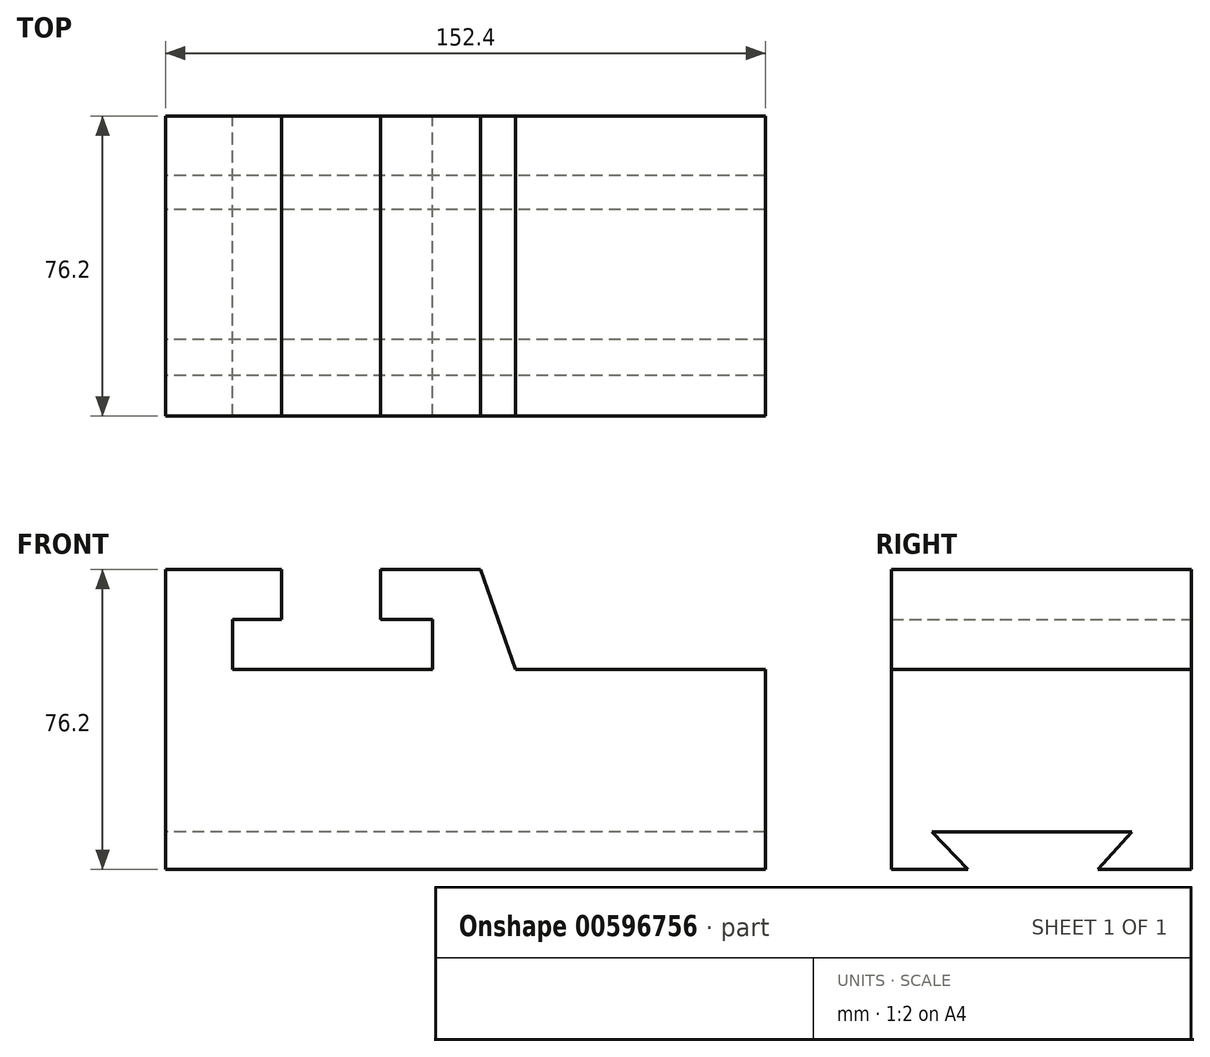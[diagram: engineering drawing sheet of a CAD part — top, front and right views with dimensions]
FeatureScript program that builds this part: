
annotation { "Feature Type Name" : "Feature", "Feature Type Description" : "" }
export const myFeature = defineFeature(function(context is Context, id is Id, definition is map)
    precondition{}
    {
        {
            var Q0;
            Q0=qCreatedBy(makeId("Front.planeOp"),FACE);
            var sketch = newSketch(context, id + "F0", { "sketchPlane" : qUnion([Q0])});
            skLineSegment(sketch, "E0", {"start": v(0, 0) * mm, "end": v(152.4, 0) * mm});
            skLineSegment(sketch, "E1", {"start": v(152.4, 0) * mm, "end": v(152.4, 50.8) * mm});
            skLineSegment(sketch, "E2", {"start": v(152.4, 50.8) * mm, "end": v(88.9, 50.8) * mm});
            skLineSegment(sketch, "E3", {"start": v(88.9, 50.8) * mm, "end": v(79.98, 76.2) * mm});
            skLineSegment(sketch, "E4", {"start": v(79.98, 76.2) * mm, "end": v(54.58, 76.2) * mm});
            skLineSegment(sketch, "E5", {"start": v(54.58, 76.2) * mm, "end": v(54.58, 63.5) * mm});
            skLineSegment(sketch, "E6", {"start": v(54.58, 63.5) * mm, "end": v(67.82, 63.5) * mm});
            skLineSegment(sketch, "E7", {"start": v(67.82, 63.5) * mm, "end": v(67.82, 50.8) * mm});
            skLineSegment(sketch, "E8", {"start": v(67.82, 50.8) * mm, "end": v(17.02, 50.8) * mm});
            skLineSegment(sketch, "E9", {"start": v(17.02, 50.8) * mm, "end": v(17.02, 63.5) * mm});
            skLineSegment(sketch, "E10", {"start": v(17.02, 63.5) * mm, "end": v(29.44, 63.5) * mm});
            skLineSegment(sketch, "E11", {"start": v(29.44, 63.5) * mm, "end": v(29.44, 76.2) * mm});
            skLineSegment(sketch, "E12", {"start": v(29.44, 76.2) * mm, "end": v(0, 76.2) * mm});
            skLineSegment(sketch, "E13", {"start": v(0, 76.2) * mm, "end": v(0, 0) * mm});
            skSolve(sketch);
        }
        {
            var Q0;
            Q0 = qSketchRegion(id + "F0", true);
            extrude(context, id + "F1", {"entities" : qUnion([Q0]), "depth" : 76.2 * mm, "offsetDistance" : 25.4 * mm});
        }
        {
            var Q0;
            Q0=qCreatedBy(makeId("Right.planeOp"),FACE);
            var sketch = newSketch(context, id + "F2", { "sketchPlane" : qUnion([Q0])});
            skLineSegment(sketch, "E14", {"start": v(-23.75, 0) * mm, "end": v(-15.11, 9.53) * mm});
            skLineSegment(sketch, "E15", {"start": v(-15.11, 9.53) * mm, "end": v(-65.91, 9.53) * mm});
            skLineSegment(sketch, "E16", {"start": v(-65.91, 9.53) * mm, "end": v(-56.77, 0) * mm});
            skLineSegment(sketch, "E17", {"start": v(-56.77, 0) * mm, "end": v(-23.75, 0) * mm});
            skSolve(sketch);
        }
        {
            var Q0;
            Q0 = qSketchRegion(id + "F2", true);
            extrude(context, id + "F3", {"entities" : qUnion([Q0]), "operationType" : NewBodyOperationType.REMOVE, "depth" : 182.63 * mm, "offsetDistance" : 25.4 * mm});
        }
    });
